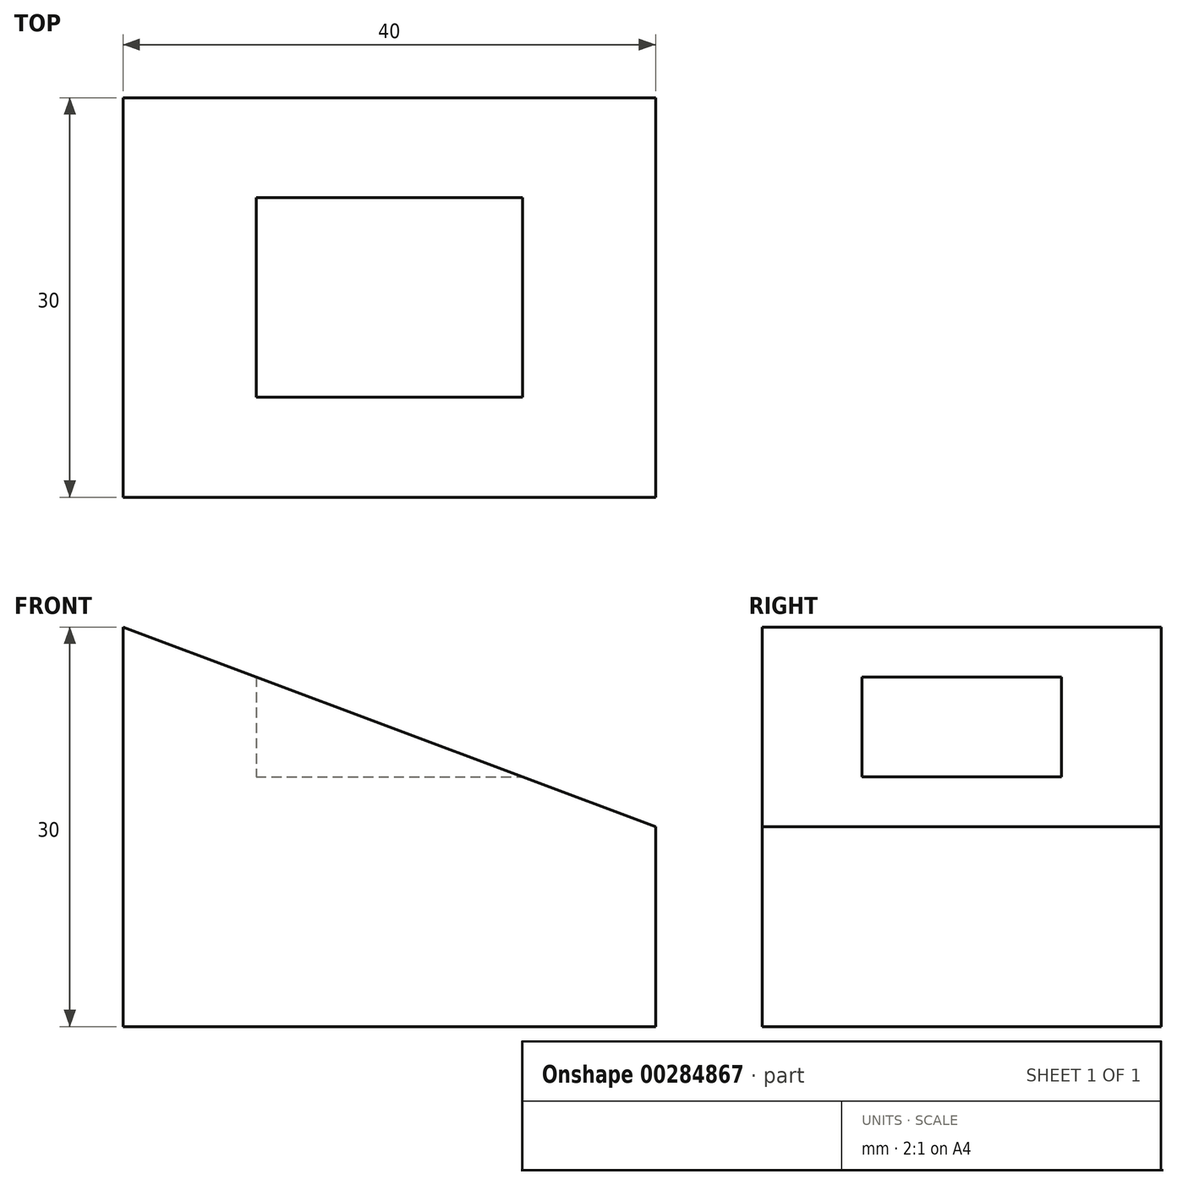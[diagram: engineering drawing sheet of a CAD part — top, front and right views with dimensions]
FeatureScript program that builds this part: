
annotation { "Feature Type Name" : "Feature", "Feature Type Description" : "" }
export const myFeature = defineFeature(function(context is Context, id is Id, definition is map)
    precondition{}
    {
        {
            var Q0;
            Q0=qCreatedBy(makeId("Front.planeOp"),FACE);
            var sketch = newSketch(context, id + "F0", { "sketchPlane" : qUnion([Q0])});
            skLineSegment(sketch, "E0.bottom", {"start": v(0, 0) * mm, "end": v(40, 0) * mm});
            skLineSegment(sketch, "E0.top", {"start": v(0, 30) * mm, "end": v(40, 30) * mm});
            skLineSegment(sketch, "E0.left", {"start": v(0, 0) * mm, "end": v(0, 30) * mm});
            skLineSegment(sketch, "E0.right", {"start": v(40, 0) * mm, "end": v(40, 30) * mm});
            skLineSegment(sketch, "E1", {"start": v(0, 30) * mm, "end": v(40, 15) * mm});
            skLineSegment(sketch, "E2.bottom", {"start": v(10, 26.25) * mm, "end": v(30, 26.25) * mm});
            skLineSegment(sketch, "E2.top", {"start": v(10, 18.75) * mm, "end": v(30, 18.75) * mm});
            skLineSegment(sketch, "E2.left", {"start": v(10, 26.25) * mm, "end": v(10, 18.75) * mm});
            skLineSegment(sketch, "E2.right", {"start": v(30, 26.25) * mm, "end": v(30, 18.75) * mm});
            skSolve(sketch);
        }
        {
            var Q0;
            {var subQ4=sQuery(id+"F0.wireOp",EDGE,"E0.bottom");Q0=makeQuery(id+"F0.imprint","IMPRINT",FACE,{"disambiguationData":[TD([[makeQuery(id+"F0.imprint","IMPRINT",EDGE,{"derivedFrom":subQ4}),1.0]])]});}
            var Q1;
            {var subQ2=sQuery(id+"F0.wireOp",EDGE,"E2.top");Q1=makeQuery(id+"F0.imprint","IMPRINT",FACE,{"disambiguationData":[TD([[makeQuery(id+"F0.imprint","IMPRINT",EDGE,{"derivedFrom":subQ2}),1.0]])]});}
            extrude(context, id + "F1", {"entities" : qUnion([Q0, Q1]), "depth" : 30 * mm, "symmetric" : true});
        }
        {
            var Q0;
            {var subQ2=sQuery(id+"F0.wireOp",EDGE,"E2.top");Q0=makeQuery(id+"F0.imprint","IMPRINT",FACE,{"disambiguationData":[TD([[makeQuery(id+"F0.imprint","IMPRINT",EDGE,{"derivedFrom":subQ2}),1.0]])]});}
            extrude(context, id + "F2", {"entities" : qUnion([Q0]), "operationType" : NewBodyOperationType.REMOVE, "oppositeDirection" : true, "depth" : 15 * mm, "symmetric" : true});
        }
    });
